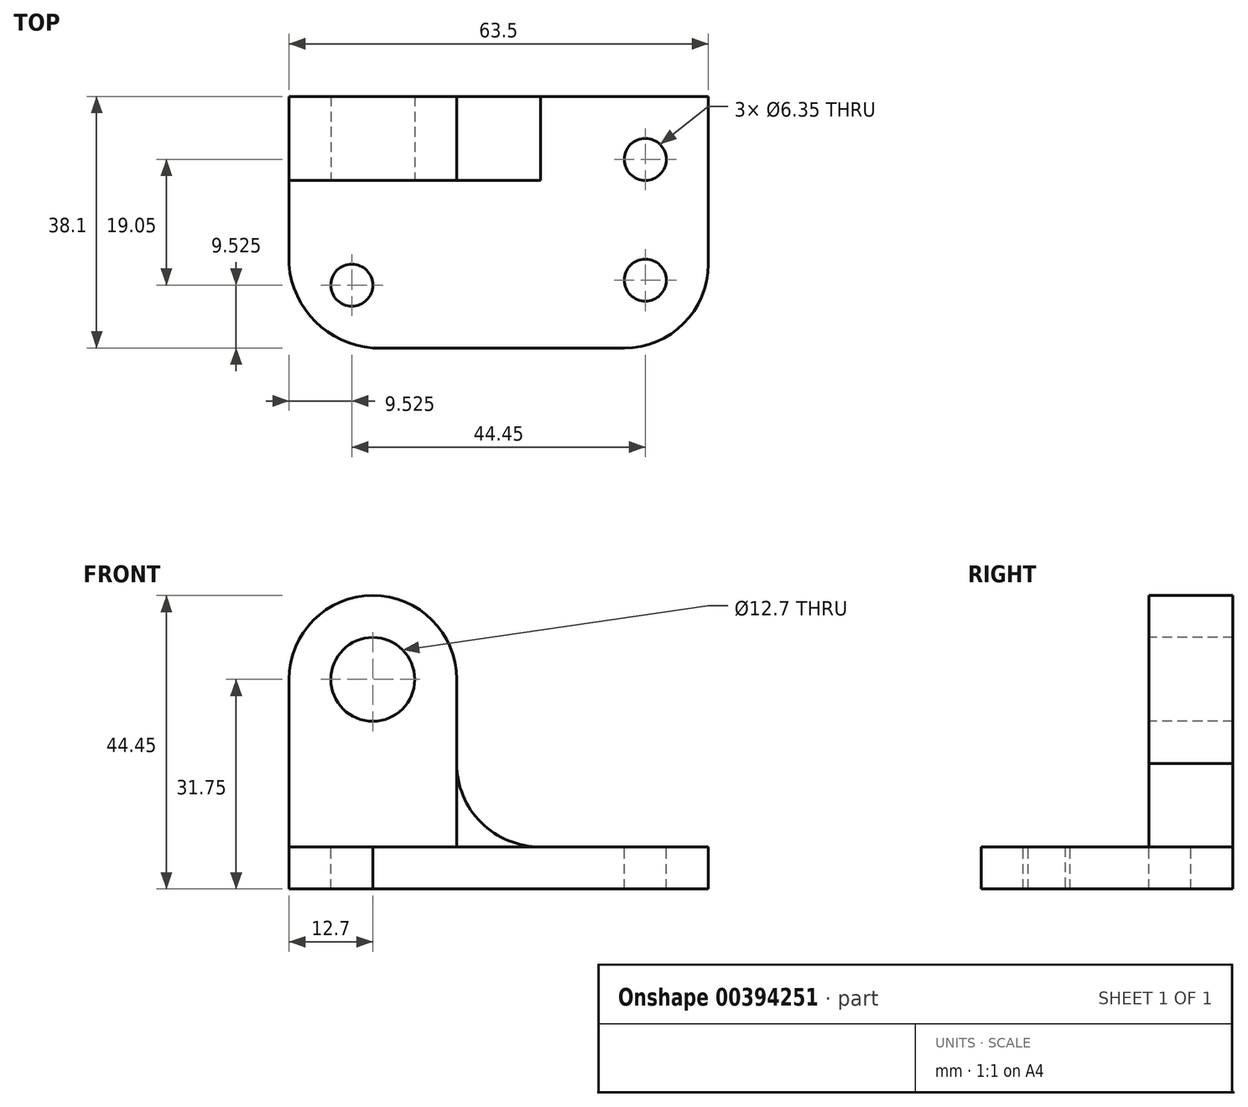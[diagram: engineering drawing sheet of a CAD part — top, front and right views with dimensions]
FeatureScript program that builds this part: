
annotation { "Feature Type Name" : "Feature", "Feature Type Description" : "" }
export const myFeature = defineFeature(function(context is Context, id is Id, definition is map)
    precondition{}
    {
        {
            var Q0;
            Q0=qCreatedBy(makeId("Top.planeOp"),FACE);
            var sketch = newSketch(context, id + "F0", { "sketchPlane" : qUnion([Q0])});
            skLineSegment(sketch, "E0", {"start": v(0, 38.1) * mm, "end": v(63.5, 38.1) * mm});
            skLineSegment(sketch, "E1", {"start": v(63.5, 38.1) * mm, "end": v(63.5, 0) * mm});
            skLineSegment(sketch, "E2", {"start": v(63.5, 0) * mm, "end": v(0, 0) * mm});
            skLineSegment(sketch, "E3", {"start": v(0, 0) * mm, "end": v(0, 38.1) * mm});
            skArc(sketch, "E4", {"start": v(50.8, 0) * mm, "mid": v(59.78, 3.72) * mm, "end": v(63.5, 12.7) * mm});
            skArc(sketch, "E5", {"start": v(0, 12.7) * mm, "mid": v(4, 4) * mm, "end": v(12.7, 0) * mm});
            skSolve(sketch);
        }
        {
            var Q0;
            {var subQ1=sQuery(id+"F0.wireOp",EDGE,"E0");Q0=makeQuery(id+"F0.imprint","IMPRINT",FACE,{"disambiguationData":[TD([[makeQuery(id+"F0.imprint","IMPRINT",EDGE,{"derivedFrom":subQ1}),-1.0]])]});}
            extrude(context, id + "F1", {"entities" : qUnion([Q0]), "depth" : 6.35 * mm});
        }
        {
            var Q0;
            Q0=makeQuery(id+"F1.opExtrude","CAP_FACE",FACE,{"disambiguationData":[OSD([sQuery(id+"F0.wireOp",EDGE,"E0"),sQuery(id+"F0.wireOp",EDGE,"E1"),sQuery(id+"F0.wireOp",EDGE,"E2"),sQuery(id+"F0.wireOp",EDGE,"E3"),sQuery(id+"F0.wireOp",EDGE,"E4"),sQuery(id+"F0.wireOp",EDGE,"E5")])],"isStart":false});
            var sketch = newSketch(context, id + "F2", { "sketchPlane" : qUnion([Q0])});
            skCircle(sketch, "E6", {"center": v(9.52, 9.52) * mm, "radius": 3.18 * mm});
            skCircle(sketch, "E7", {"center": v(53.98, 10.28) * mm, "radius": 3.18 * mm});
            skCircle(sketch, "E8", {"center": v(53.98, 28.57) * mm, "radius": 3.18 * mm});
            skSolve(sketch);
        }
        {
            var Q0;
            Q0=makeQuery(id+"F2.imprint","IMPRINT",FACE,{"disambiguationData":[TD([[makeQuery(id+"F2.imprint","IMPRINT",EDGE,{"derivedFrom":sQuery(id+"F2.wireOp",EDGE,"E6")}),1.0]])]});
            var Q1;
            Q1=makeQuery(id+"F2.imprint","IMPRINT",FACE,{"disambiguationData":[TD([[makeQuery(id+"F2.imprint","IMPRINT",EDGE,{"derivedFrom":sQuery(id+"F2.wireOp",EDGE,"E7")}),1.0]])]});
            var Q2;
            Q2=makeQuery(id+"F2.imprint","IMPRINT",FACE,{"disambiguationData":[TD([[makeQuery(id+"F2.imprint","IMPRINT",EDGE,{"derivedFrom":sQuery(id+"F2.wireOp",EDGE,"E8")}),1.0]])]});
            extrude(context, id + "F3", {"entities" : qUnion([Q0, Q1, Q2]), "operationType" : NewBodyOperationType.REMOVE, "oppositeDirection" : true, "depth" : 6.35 * mm});
        }
        {
            var Q0;
            Q0=makeQuery(id+"F1.opExtrude","SWEPT_FACE",FACE,{"disambiguationData":[OSD([sQuery(id+"F0.wireOp",EDGE,"E0")])]});
            var sketch = newSketch(context, id + "F4", { "sketchPlane" : qUnion([Q0])});
            skLineSegment(sketch, "E9", {"start": v(0, 6.35) * mm, "end": v(0, 44.45) * mm});
            skLineSegment(sketch, "E10", {"start": v(0, 44.45) * mm, "end": v(-25.4, 44.45) * mm});
            skLineSegment(sketch, "E11", {"start": v(-25.4, 44.45) * mm, "end": v(-25.4, 6.35) * mm});
            skLineSegment(sketch, "E12", {"start": v(-25.4, 6.35) * mm, "end": v(0, 6.35) * mm});
            skArc(sketch, "E13", {"start": v(0, 31.75) * mm, "mid": v(-12.7, 44.45) * mm, "end": v(-25.4, 31.75) * mm});
            skSolve(sketch);
        }
        {
            var Q0;
            {var subQ2=sQuery(id+"F4.wireOp",EDGE,"E12");Q0=makeQuery(id+"F4.imprint","IMPRINT",FACE,{"disambiguationData":[TD([[makeQuery(id+"F4.imprint","IMPRINT",EDGE,{"derivedFrom":subQ2}),1.0]])]});}
            var sketch = newSketch(context, id + "F5", { "sketchPlane" : qUnion([Q0])});
            skLineSegment(sketch, "E14", {"start": v(-25.4, 6.31) * mm, "end": v(-25.4, 19.01) * mm});
            skLineSegment(sketch, "E15", {"start": v(-25.4, 19.01) * mm, "end": v(-38.1, 19.01) * mm});
            skLineSegment(sketch, "E16", {"start": v(-38.1, 19.01) * mm, "end": v(-38.1, 6.39) * mm});
            skLineSegment(sketch, "E17", {"start": v(-38.1, 6.39) * mm, "end": v(-25.4, 6.31) * mm});
            skArc(sketch, "E18", {"start": v(-38.1, 6.39) * mm, "mid": v(-29.12, 10.06) * mm, "end": v(-25.4, 19.01) * mm});
            skSolve(sketch);
        }
        {
            var Q0;
            {var subQ6=sQuery(id+"F5.wireOp",EDGE,"E18");Q0=makeQuery(id+"F5.imprint","IMPRINT",FACE,{"disambiguationData":[TD([[makeQuery(id+"F5.imprint","IMPRINT",EDGE,{"derivedFrom":subQ6}),-1.0]])]});}
            var Q1;
            {var subQ4=sQuery(id+"F4.wireOp",EDGE,"E12");Q1=makeQuery(id+"F4.imprint","IMPRINT",FACE,{"disambiguationData":[TD([[makeQuery(id+"F4.imprint","IMPRINT",EDGE,{"derivedFrom":subQ4}),-1.0]])]});}
            extrude(context, id + "F6", {"entities" : qUnion([Q0, Q1]), "oppositeDirection" : true, "depth" : 12.7 * mm});
        }
        {
            var Q0;
            Q0=makeQuery(id+"F6.opExtrude","CAP_FACE",FACE,{"disambiguationData":[OSD([sQuery(id+"F4.wireOp",EDGE,"E9"),sQuery(id+"F4.wireOp",EDGE,"E11"),sQuery(id+"F4.wireOp",EDGE,"E12"),sQuery(id+"F4.wireOp",EDGE,"E13")])],"isStart":false});
            var sketch = newSketch(context, id + "F7", { "sketchPlane" : qUnion([Q0])});
            skCircle(sketch, "E19", {"center": v(12.7, 31.75) * mm, "radius": 6.35 * mm});
            skSolve(sketch);
        }
        {
            var Q0;
            Q0=makeQuery(id+"F7.imprint","IMPRINT",FACE,{"disambiguationData":[TD([[makeQuery(id+"F7.imprint","IMPRINT",EDGE,{"derivedFrom":sQuery(id+"F7.wireOp",EDGE,"E19")}),1.0]])]});
            extrude(context, id + "F8", {"entities" : qUnion([Q0]), "operationType" : NewBodyOperationType.REMOVE, "oppositeDirection" : true, "depth" : 12.7 * mm});
        }
    });
